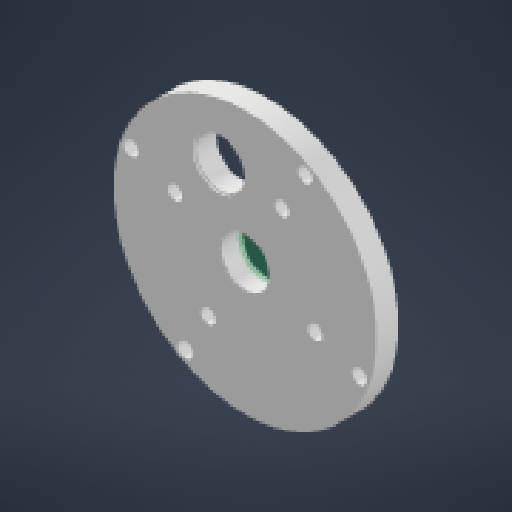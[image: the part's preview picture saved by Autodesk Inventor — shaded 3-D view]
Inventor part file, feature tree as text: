
AUTODESK INVENTOR PART (.ipt)
format: ipt  version: 2024.2 (Build 282272000, 272)  size: 207,360 bytes
history: native  units: in
note: dims shown in document units (in); Inventor stores cm internally (conversion verified against a paired STEP export)
features: reference x15, other x9, sketch x6, extrude x6, plane x2
ambient origin geometry x8: Origin, YZ Plane, XZ Plane, XY Plane, X Axis, Y Axis, Z Axis, Center Point
bodies: Solid1 (feature_tree)
feature tree (38):
  sketch  "Sketch1"  dims[d0=0.1693in d1=0.1693in]
  plane  "Work Plane1"
  extrude  "Extrusion1"  Depth=0.1693in
  plane  "Work Plane2"
  extrude  "Extrusion3"  Depth=0.1693in
  extrude  "Extrusion4"  Depth=0.0197in TaperAngle=0.0deg
  extrude  "Extrusion5"  Depth=0.5906in
  extrude  "Extrusion6"  Depth=0.002in
  extrude  "Extrusion7"  Depth=0.15in
  reference  "Reference1"
  reference  "Reference2"
  reference  "Reference3"
  reference  "Reference4"
  reference  "Reference5"
  reference  "Reference6"
  reference  "Reference7"
  sketch  "Sketch3"  dims[d2=0.1693in d3=0.1693in]
  reference  "Reference9"
  sketch  "Sketch5"  dims[d4=1.0in d5=0.0in d8=0.0197in d9=0.0in]
  reference  "Reference10"
  sketch  "Sketch6"  dims[d10=0.5906in d11=0.5906in]
  reference  "Reference11"
  reference  "Reference12"
  reference  "Reference13"
  reference  "Reference14"
  sketch  "Sketch7"  dims[d12=0.002in d13=0.0in d16=0.1693in]
  reference  "Reference15"
  reference  "Reference16"
  sketch  "Sketch8"  dims[d17=0.1693in d18=1.3944in d19=1.3944in d20=0.0in d21=0.1693in d22=0.1693in d23=0.0in d24=1.3944in d25=1.3944in d26=0.0in d27=0.002in d28=0.0in d29=0.315in d30=0.315in d31=0.15in d32=0.0in d33=0.1693in d34=0.1693in d35=0.0in d36=0.0in]
  other  "<userpath>\Desktop\Robotics\Swerve2\Assemblies\Pod.iam"
  other  "Pod.iam"
  other  "3ID3.5OD_Bearing:1"
  parser-record x1  (decoder bookkeeping rows leaked as tree rows — omitted from the tree; the rows remain in map.json)
  other  "1501 Series M4 x 0.7mm Standoff (6mm OD, 8mm Length) - 4 Pack:4"
  other  "1501 Series M4 x 0.7mm Standoff (6mm OD, 8mm Length) - 4 Pack:3"
  other  "1501 Series M4 x 0.7mm Standoff (6mm OD, 8mm Length) - 4 Pack:2"
  other  "1501 Series M4 x 0.7mm Standoff (6mm OD, 8mm Length) - 4 Pack:1"
  other  "Wheel_Axle_Holder:1"
